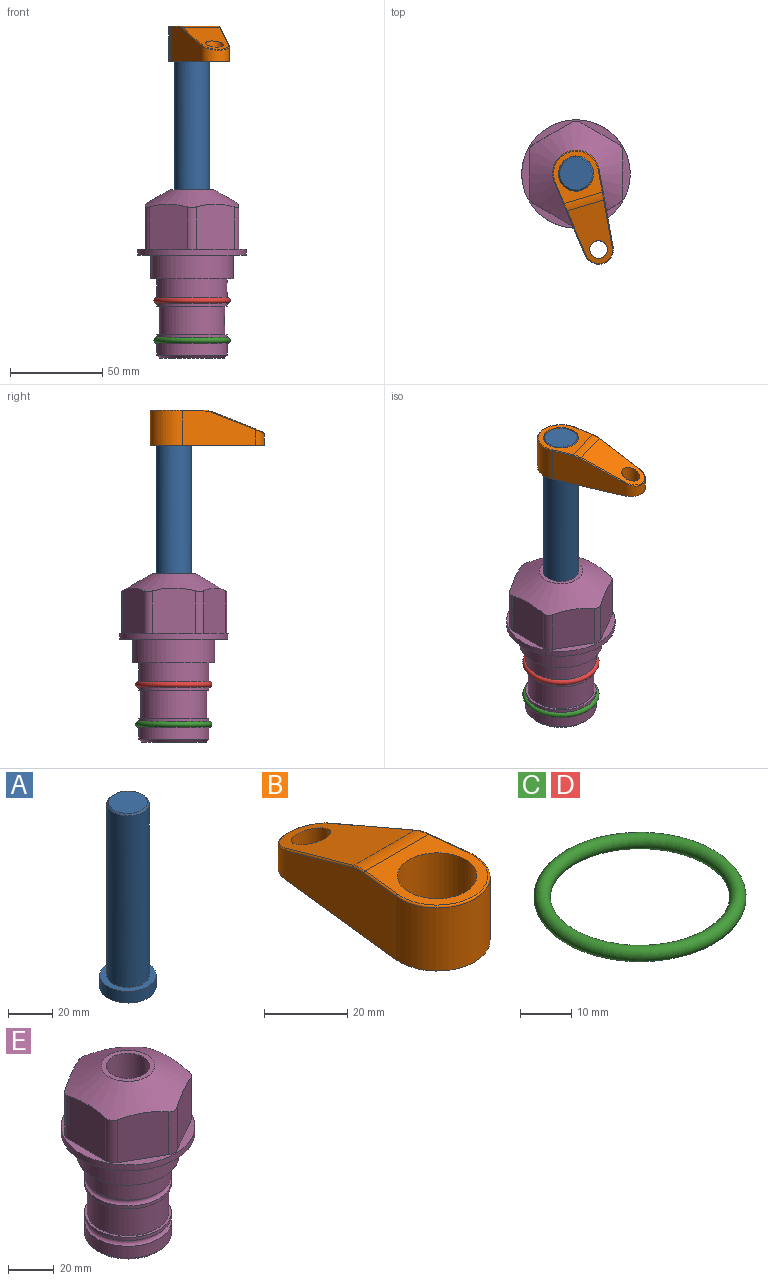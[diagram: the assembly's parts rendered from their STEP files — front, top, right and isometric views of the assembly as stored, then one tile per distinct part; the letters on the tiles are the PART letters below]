
ASSEMBLY  parts=5 mates=3
PART A: 6 faces, bbox 25.4x25.4x101.6 mm
  f0: plane 17.46x17.46mm, normal (0,0,1), area 239.5mm2, adj f5
  f1: plane 25.4x25.4mm, normal (0,0,-1), area 506.7mm2, adj f2
  f2: cylinder r=12.7mm len=25.4mm, axis (0,0,1), area 506.7mm2, adj f1,f3
  f3: plane 25.4x25.4mm, normal (0,0,1), area 221.7mm2, adj f2,f4
  f4: cylinder r=9.53mm len=94.46mm, axis (0,0,1), area 5653mm2, adj f3,f5
  f5: cone r=8.73mm half-angle=45deg, axis (0,0,-1), area 64.4mm2, adj f0,f4
PART B: 44 faces, bbox 27.5x64.5x19.1 mm
  f0: plane 2.3x0.95mm, normal (0,0,-1), area 1mm2, adj f25,f30,f34
  f1: plane 63.5x25.4mm, normal (0,0,-1), area 561.7mm2, adj f2,f3,f4,f5,f6,f7,f19,f20
  f2: cylinder r=12.7mm len=25.4mm, axis (0,0,-1), area 792.2mm2, adj f1,f3,f5,f13
  f3: plane 42.33x18.54mm, normal (0.99,0.11,0), area 647mm2, adj f1,f2,f4,f11,f12,f14
  f4: cylinder r=7.94mm len=15.78mm, axis (0,0,-1), area 158.6mm2, adj f1,f3,f5,f16
  f5: plane 42.33x18.54mm, normal (-0.99,0.11,0), area 647mm2, adj f1,f2,f4,f15,f17,f18
  f6: cylinder r=9.53mm len=19.05mm, axis (0,0,-1), area 1140.1mm2, adj f1,f8
  f7: cylinder r=4.76mm len=10.98mm, axis (0,0,-1), area 276.1mm2, adj f1,f9
  f8: plane 25.83x24.38mm, normal (0,0,1), area 262.2mm2, adj f6,f10,f11,f13,f15
  f9: plane 32.49x20.55mm, normal (0,0.34,0.94), area 489.9mm2, adj f7,f10,f14,f16,f18
  f10: cylinder r=12.7mm len=21.49mm, axis (-1,0,0), area 93.2mm2, adj f8,f9,f12,f17
  f11: cylinder r=0.51mm len=12.34mm, axis (0.11,-0.99,0), area 9.9mm2, adj f3,f8,f12,f13
  f12: bspline ~7.62x1.64mm, area 3.5mm2, adj f3,f10,f11,f14
  f13: torus R=12.19mm, axis (0,0,1), area 33.6mm2, adj f2,f8,f11,f15
  f14: cylinder r=0.51mm len=26.01mm, axis (0.1,-0.93,0.34), area 21.6mm2, adj f3,f9,f12,f16
  f15: cylinder r=0.51mm len=12.34mm, axis (0.11,0.99,0), area 9.9mm2, adj f5,f8,f13,f17
  f16: bspline ~15.78x7.05mm, area 15.7mm2, adj f4,f9,f14,f18
  f17: bspline ~7.62x1.64mm, area 3.5mm2, adj f5,f10,f15,f18
  f18: cylinder r=0.51mm len=26.01mm, axis (0.1,0.93,-0.34), area 21.6mm2, adj f5,f9,f16,f17
  f19: plane 21.6x14.29mm, normal (-0.99,-0.11,0), area 242.6mm2, adj f1,f26,f28,f34,f36,f38
  f20: plane 21.6x14.29mm, normal (0.99,-0.11,0), area 242.6mm2, adj f1,f27,f29,f37,f39,f41
  f21: cylinder r=12.7mm len=14.29mm, axis (0,0,-1), area 173.2mm2, adj f1,f26,f27,f30,f31,f33
  f22: cylinder r=7.94mm len=7.63mm, axis (0,0,-1), area 53.8mm2, adj f1,f28,f29,f42
  f23: plane 2.3x0.95mm, normal (0,0,-1), area 1mm2, adj f25,f33,f37
  f24: plane 17.94x12.32mm, normal (0,-0.34,-0.94), area 191.2mm2, adj f25,f38,f41,f42
  f25: cylinder r=9.53mm len=12.93mm, axis (-1,0,0), area 37.5mm2, adj f0,f23,f24,f31,f36,f39
  f26: cylinder r=1.59mm len=14.29mm, axis (0,0,-1), area 49mm2, adj f1,f19,f21,f32
  f27: cylinder r=1.59mm len=14.29mm, axis (0,0,-1), area 49mm2, adj f1,f20,f21,f35
  f28: cylinder r=1.59mm len=7.28mm, axis (0,0,-1), area 22.1mm2, adj f1,f19,f22,f40
  f29: cylinder r=1.59mm len=7.28mm, axis (0,0,-1), area 22.1mm2, adj f1,f20,f22,f43
  f30: torus R=14.29mm, axis (0,0,1), area 5.8mm2, adj f0,f21,f31,f32
  f31: bspline ~11.06x2.73mm, area 20.8mm2, adj f21,f25,f30,f33
  f32: sphere r=1.59mm, area 5.4mm2, adj f26,f30,f34
  f33: torus R=14.29mm, axis (0,0,1), area 5.8mm2, adj f21,f23,f31,f35
  f34: cylinder r=1.59mm len=1.68mm, axis (-0.11,0.99,0), area 2.4mm2, adj f0,f19,f32,f36
  f35: sphere r=1.59mm, area 5.4mm2, adj f27,f33,f37
  f36: bspline ~5.82x2.33mm, area 7.7mm2, adj f19,f25,f34,f38
  f37: cylinder r=1.59mm len=1.68mm, axis (0.11,0.99,0), area 2.4mm2, adj f20,f23,f35,f39
  f38: cylinder r=1.59mm len=18.33mm, axis (0.1,-0.93,0.34), area 46.7mm2, adj f19,f24,f36,f40
  f39: bspline ~5.82x2.33mm, area 7.7mm2, adj f20,f25,f37,f41
  f40: sphere r=1.59mm, area 3.6mm2, adj f28,f38,f42
  f41: cylinder r=1.59mm len=18.33mm, axis (0.1,0.93,-0.34), area 46.7mm2, adj f20,f24,f39,f43
  f42: bspline ~8.31x1.84mm, area 15.3mm2, adj f22,f24,f40,f43
  f43: sphere r=1.59mm, area 3.6mm2, adj f29,f41,f42
PART C: 1 faces, bbox 44.7x44.7x3.2 mm
  f0: torus R=19.05mm, axis (0,0,1), area 1193.9mm2
PART D: same geometry as C
PART E: 36 faces, bbox 58.7x58.7x91.2 mm
  f0: cylinder r=17.78mm len=35.56mm, axis (0,0,1), area 1670.8mm2, adj f23,f24,f31
  f1: cylinder r=19.05mm len=38.1mm, axis (0,0,1), area 1191.9mm2, adj f26,f27,f30
  f2: plane 58.66x58.66mm, normal (0,0,-1), area 1150.6mm2, adj f3,f28
  f3: cylinder r=29.33mm len=58.66mm, axis (0,0,-1), area 585.1mm2, adj f2,f4
  f4: plane 58.66x58.66mm, normal (0,0,1), area 475.9mm2, adj f3,f5,f6,f7,f8,f9,f10,f11
  f5: plane 24.5x20.32mm, normal (-0.5,0.87,0), area 562.8mm2, adj f4,f15,f16,f17
  f6: plane 24.5x20.32mm, normal (0.5,0.87,0), area 562.8mm2, adj f4,f14,f15,f17
  f7: plane 24.5x23.48mm, normal (1,0,0), area 562.8mm2, adj f4,f13,f14,f17
  f8: plane 24.5x20.32mm, normal (0.5,-0.87,0), area 562.8mm2, adj f4,f12,f13,f17
  f9: plane 24.5x20.32mm, normal (-0.5,-0.87,0), area 562.8mm2, adj f4,f11,f12,f17
  f10: plane 24.5x23.48mm, normal (-1,0,0), area 562.8mm2, adj f4,f11,f16,f17
  f11: cylinder r=5.08mm len=23.01mm, axis (0,0,-1), area 121.2mm2, adj f4,f9,f10,f17
  f12: cylinder r=5.08mm len=23.01mm, axis (0,0,-1), area 121.2mm2, adj f4,f8,f9,f17
  f13: cylinder r=5.08mm len=23.01mm, axis (0,0,-1), area 121.2mm2, adj f4,f7,f8,f17
  f14: cylinder r=5.08mm len=23.01mm, axis (0,0,-1), area 121.2mm2, adj f4,f6,f7,f17
  f15: cylinder r=5.08mm len=23.01mm, axis (0,0,-1), area 121.2mm2, adj f4,f5,f6,f17
  f16: cylinder r=5.08mm len=23.01mm, axis (0,0,-1), area 121.2mm2, adj f4,f5,f10,f17
  f17: cone r=11.73mm half-angle=60deg, axis (0,0,-1), area 2071.8mm2, adj f5,f6,f7,f8,f9,f10,f11,f12
  f18: plane 23.46x23.46mm, normal (0,0,1), area 147.4mm2, adj f17,f35
  f19: plane 34.93x34.93mm, normal (0,0,-1), area 958mm2, adj f29
  f20: cylinder r=19.05mm len=38.1mm, axis (0,0,1), area 760.1mm2, adj f21,f29
  f21: torus R=19.05mm, axis (0,0,1), area 565.3mm2, adj f20,f22
  f22: cylinder r=19.05mm len=38.1mm, axis (0,0,1), area 190mm2, adj f21,f23
  f23: plane 38.1x38.1mm, normal (0,0,1), area 146.9mm2, adj f0,f22
  f24: plane 38.1x38.1mm, normal (0,0,-1), area 146.9mm2, adj f0,f25
  f25: cylinder r=19.05mm len=38.1mm, axis (0,0,1), area 190mm2, adj f24,f26
  f26: torus R=19.05mm, axis (0,0,1), area 565.3mm2, adj f1,f25
  f27: plane 44.45x44.45mm, normal (0,0,-1), area 411.7mm2, adj f1,f28
  f28: cylinder r=22.23mm len=44.45mm, axis (0,0,1), area 1773.5mm2, adj f2,f27
  f29: cone r=19.05mm half-angle=45deg, axis (0,0,1), area 257.5mm2, adj f19,f20
  f30: cylinder r=3.17mm len=6.75mm, axis (-1,0,0), area 128mm2, adj f1,f33
  f31: cylinder r=3.17mm len=6.35mm, axis (-1,0,0), area 102.5mm2, adj f0,f33
  f32: plane 25.4x25.4mm, normal (0,0,1), area 506.7mm2, adj f33
  f33: cylinder r=12.7mm len=66.42mm, axis (0,0,-1), area 5236.2mm2, adj f30,f31,f32,f34
  f34: cone r=9.53mm half-angle=30deg, axis (0,0,-1), area 443.4mm2, adj f33,f35
  f35: cylinder r=9.53mm len=19.05mm, axis (0,0,-1), area 849mm2, adj f18,f34
PLACE A rot(axis=(0,0,-1),73.4deg) t=(0,0,50.4)mm
PLACE B rot(axis=(0,0,-1),163.4deg) t=(0,0,105.01)mm
PLACE C t=(0,0,-21.59)mm
PLACE D at identity
PLACE E at identity fixed
MATE fastened C.f0 <-> E.f0  axis (0,0,1) through (0,0,-46.1)mm
MATE cylindrical A.f2 <-> E.f0  axis (0,0,1) through (0,0,76.04)mm
MATE fastened B.f2 <-> A.f2  axis (0,0,1) through (0,0,124.06)mm
